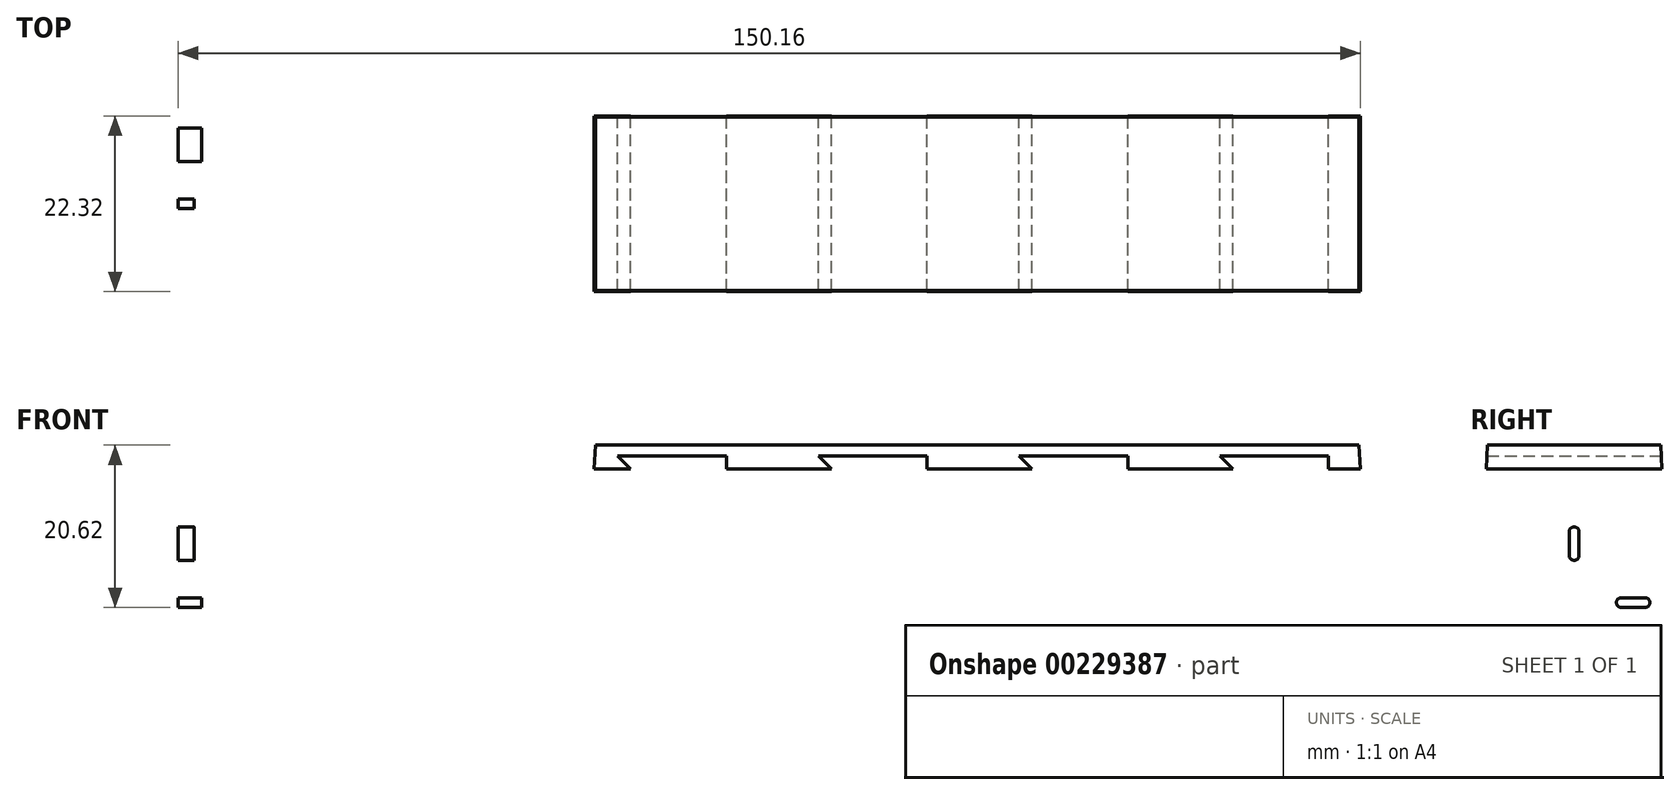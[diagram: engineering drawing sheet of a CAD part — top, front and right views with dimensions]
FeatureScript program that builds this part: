
annotation { "Feature Type Name" : "Feature", "Feature Type Description" : "" }
export const myFeature = defineFeature(function(context is Context, id is Id, definition is map)
    precondition{}
    {
        {
            var Q0;
            Q0=qCreatedBy(makeId("Top.planeOp"),FACE);
            var sketch = newSketch(context, id + "F0", { "sketchPlane" : qUnion([Q0])});
            skLineSegment(sketch, "E0", {"start": v(-75, 15.5) * mm, "end": v(-75, -15.5) * mm});
            skLineSegment(sketch, "E1", {"start": v(-75, -15.5) * mm, "end": v(75, -14) * mm});
            skLineSegment(sketch, "E2", {"start": v(75, -14) * mm, "end": v(75, 14) * mm});
            skLineSegment(sketch, "E3", {"start": v(75, 14) * mm, "end": v(-75, 15.5) * mm});
            skPoint(sketch, "E4", {"position": v(-75, 0) * mm});
            skPoint(sketch, "E5", {"position": v(75, 0) * mm});
            skPoint(sketch, "E6", {"position": v(0, 14.75) * mm});
            skLineSegment(sketch, "E7.0", {"start": v(-72, -12.47) * mm, "end": v(75, -11) * mm});
            skLineSegment(sketch, "E7.1", {"start": v(-72, 12.47) * mm, "end": v(-72, -12.47) * mm});
            skLineSegment(sketch, "E7.2", {"start": v(75, 11) * mm, "end": v(-72, 12.47) * mm});
            skLineSegment(sketch, "E8", {"start": v(-22, 11.97) * mm, "end": v(-22, -11.97) * mm});
            skSolve(sketch);
        }
        {
            var Q0;
            Q0=qCreatedBy(makeId("Top.planeOp"),FACE);
            cPlane(context, id + "F1", {"entities" : qUnion([Q0]), "cplaneType" : CPlaneType.OFFSET, "offset" : 40 * mm, "width" : 150 * mm, "height" : 150 * mm});
        }
        {
            var Q0;
            Q0=qCreatedBy(id+"F1.planeOp",FACE);
            var sketch = newSketch(context, id + "F8", { "sketchPlane" : qUnion([Q0])});
            skLineSegment(sketch, "E9.0", {"start": v(75, -14) * mm, "end": v(75, 14) * mm});
            skPoint(sketch, "E10.0", {"position": v(-75, 0) * mm});
            skLineSegment(sketch, "E11", {"start": v(75, 14) * mm, "end": v(-75, 14) * mm});
            skLineSegment(sketch, "E12", {"start": v(-75, -14) * mm, "end": v(75, -14) * mm});
            skLineSegment(sketch, "E13", {"start": v(-75, 14) * mm, "end": v(-75, -14) * mm});
            skLineSegment(sketch, "E14.0", {"start": v(-72, -11) * mm, "end": v(75, -11) * mm});
            skLineSegment(sketch, "E14.1", {"start": v(-72, 11) * mm, "end": v(-72, -11) * mm});
            skLineSegment(sketch, "E14.2", {"start": v(75, 11) * mm, "end": v(-72, 11) * mm});
            skLineSegment(sketch, "E15", {"start": v(-22, 11) * mm, "end": v(-22, -11) * mm});
            skSolve(sketch);
        }
        {
            var Q0;
            Q0=makeQuery(id+"F0.imprint","IMPRINT",FACE,{"disambiguationData":[TD([[makeQuery(id+"F0.imprint","IMPRINT",EDGE,{"derivedFrom":sQuery(id+"F0.wireOp",EDGE,"E0")}),1.0]])]});
            var Q1;
            {var subQ1=sQuery(id+"F8.wireOp",EDGE,"E11");Q1=makeQuery(id+"F8.imprint","IMPRINT",FACE,{"disambiguationData":[TD([[makeQuery(id+"F8.imprint","IMPRINT",EDGE,{"derivedFrom":subQ1}),1.0]])]});}
            loft(context, id + "F2", {"sheetProfilesArray" : [{ "sheetProfileEntities" : qUnion([Q0]) }, { "sheetProfileEntities" : qUnion([Q1]) }]});
        }
        {
            var Q0;
            {var subQ0=sQuery(id+"F0.wireOp",EDGE,"E7.1");Q0=makeQuery(id+"F0.imprint","IMPRINT",FACE,{"disambiguationData":[TD([[makeQuery(id+"F0.imprint","IMPRINT",EDGE,{"derivedFrom":subQ0}),1.0]])]});}
            extrude(context, id + "F9", {"entities" : qUnion([Q0]), "operationType" : NewBodyOperationType.ADD, "depth" : 3 * mm, "hasDraft" : true, "draftAngle" : 3 * degree});
        }
        {
            var Q0;
            Q0=makeQuery(id+"F2.opLoft","SWEPT_FACE",FACE,{"disambiguationData":[OSD([sQuery(id+"F0.wireOp",EDGE,"E0"),sQuery(id+"F0.wireOp",EDGE,"E1"),sQuery(id+"F0.wireOp",EDGE,"E3"),sQuery(id+"F8.wireOp",EDGE,"E11"),sQuery(id+"F8.wireOp",EDGE,"E12"),sQuery(id+"F8.wireOp",EDGE,"E13")])]});
            var sketch = newSketch(context, id + "F3", { "sketchPlane" : qUnion([Q0])});
            skLineSegment(sketch, "E16.0", {"start": v(-14, 40) * mm, "end": v(14, 40) * mm});
            skLineSegment(sketch, "E17.0", {"start": v(15.5, 0) * mm, "end": v(14, 40) * mm});
            skLineSegment(sketch, "E18.0", {"start": v(-15.5, 0) * mm, "end": v(15.5, 0) * mm});
            skLineSegment(sketch, "E19.0", {"start": v(-15.5, 0) * mm, "end": v(-14, 40) * mm});
            skPoint(sketch, "E20", {"position": v(-14.75, 20) * mm});
            skPoint(sketch, "E21", {"position": v(14.75, 20) * mm});
            skPoint(sketch, "E22", {"position": v(0, 40) * mm});
            skPoint(sketch, "E23", {"position": v(0, 0) * mm});
            skPoint(sketch, "E24", {"position": v(0, 20) * mm});
            skCircle(sketch, "E25", {"center": v(0, 20) * mm, "radius": 2.5 * mm});
            skLineSegment(sketch, "E26", {"start": v(0, 26) * mm, "end": v(0, 29) * mm});
            skLineSegment(sketch, "E27", {"start": v(-9, 20) * mm, "end": v(-6, 20) * mm});
            skArc(sketch, "E28.0.startCap", {"start": v(-9, 19.37) * mm, "mid": v(-9.63, 20) * mm, "end": v(-9, 20.62) * mm});
            skArc(sketch, "E28.0.endCap", {"start": v(-6, 20.62) * mm, "mid": v(-5.38, 20) * mm, "end": v(-6, 19.37) * mm});
            skLineSegment(sketch, "E28.0.left", {"start": v(-9, 20.62) * mm, "end": v(-6, 20.62) * mm});
            skLineSegment(sketch, "E28.0.right", {"start": v(-9, 19.37) * mm, "end": v(-6, 19.37) * mm});
            skArc(sketch, "E29.0.startCap", {"start": v(0.62, 26) * mm, "mid": v(0, 25.37) * mm, "end": v(-0.62, 26) * mm});
            skArc(sketch, "E29.0.endCap", {"start": v(-0.62, 29) * mm, "mid": v(0, 29.62) * mm, "end": v(0.62, 29) * mm});
            skLineSegment(sketch, "E29.0.left", {"start": v(-0.62, 26) * mm, "end": v(-0.62, 29) * mm});
            skLineSegment(sketch, "E29.0.right", {"start": v(0.62, 26) * mm, "end": v(0.62, 29) * mm});
            skLineSegment(sketch, "E30", {"start": v(0, 40) * mm, "end": v(0, 0) * mm, "construction": true});
            skLineSegment(sketch, "E31", {"start": v(-14.75, 20) * mm, "end": v(14.75, 20) * mm, "construction": true});
            skArc(sketch, "E32.MirrorCS", {"start": v(9, 19.37) * mm, "mid": v(9.62, 20) * mm, "end": v(9, 20.62) * mm});
            skLineSegment(sketch, "E33.MirrorCS", {"start": v(9, 20.62) * mm, "end": v(6, 20.62) * mm});
            skArc(sketch, "E34.MirrorCS", {"start": v(6, 20.62) * mm, "mid": v(5.37, 20) * mm, "end": v(6, 19.37) * mm});
            skLineSegment(sketch, "E35.MirrorCS", {"start": v(9, 19.37) * mm, "end": v(6, 19.37) * mm});
            skArc(sketch, "E36.MirrorCS", {"start": v(0.63, 14) * mm, "mid": v(0, 14.62) * mm, "end": v(-0.62, 14) * mm});
            skLineSegment(sketch, "E37.MirrorCS", {"start": v(0.63, 14) * mm, "end": v(0.63, 11) * mm});
            skLineSegment(sketch, "E38.MirrorCS", {"start": v(-0.62, 14) * mm, "end": v(-0.62, 11) * mm});
            skArc(sketch, "E39.MirrorCS", {"start": v(-0.62, 11) * mm, "mid": v(0, 10.37) * mm, "end": v(0.63, 11) * mm});
            skSolve(sketch);
        }
        {
            var Q0;
            Q0=makeQuery(id+"F3.imprint","IMPRINT",FACE,{"disambiguationData":[TD([[makeQuery(id+"F3.imprint","IMPRINT",EDGE,{"derivedFrom":sQuery(id+"F3.wireOp",EDGE,"E32.MirrorCS")}),1.0]])]});
            var Q1;
            Q1=makeQuery(id+"F3.imprint","IMPRINT",FACE,{"disambiguationData":[TD([[makeQuery(id+"F3.imprint","IMPRINT",EDGE,{"derivedFrom":sQuery(id+"F3.wireOp",EDGE,"E25")}),1.0]])]});
            var Q2;
            Q2=makeQuery(id+"F3.imprint","IMPRINT",FACE,{"disambiguationData":[TD([[makeQuery(id+"F3.imprint","IMPRINT",EDGE,{"derivedFrom":sQuery(id+"F3.wireOp",EDGE,"E29.0.startCap")}),-1.0]])]});
            var Q3;
            Q3=makeQuery(id+"F3.imprint","IMPRINT",FACE,{"disambiguationData":[TD([[makeQuery(id+"F3.imprint","IMPRINT",EDGE,{"derivedFrom":sQuery(id+"F3.wireOp",EDGE,"E36.MirrorCS")}),1.0]])]});
            var Q4;
            Q4=makeQuery(id+"F3.imprint","IMPRINT",FACE,{"disambiguationData":[TD([[makeQuery(id+"F3.imprint","IMPRINT",EDGE,{"derivedFrom":sQuery(id+"F3.wireOp",EDGE,"E28.0.startCap")}),-1.0]])]});
            extrude(context, id + "F4", {"entities" : qUnion([Q0, Q1, Q2, Q3, Q4]), "operationType" : NewBodyOperationType.REMOVE, "endBound" : BoundingType.UP_TO_NEXT, "oppositeDirection" : true, "depth" : 25 * mm});
        }
        {
            var Q0;
            {var subQ5=sQuery(id+"F8.wireOp",EDGE,"E15");Q0=makeQuery(id+"F8.imprint","IMPRINT",FACE,{"disambiguationData":[TD([[makeQuery(id+"F8.imprint","IMPRINT",EDGE,{"derivedFrom":subQ5}),1.0]])]});}
            extrude(context, id + "F5", {"entities" : qUnion([Q0]), "operationType" : NewBodyOperationType.ADD, "oppositeDirection" : true, "depth" : 3 * mm, "hasDraft" : true, "draftAngle" : 3 * degree});
        }
        {
            var Q0;
            Q0=qCreatedBy(makeId("Front.planeOp"),FACE);
            var sketch = newSketch(context, id + "F6", { "sketchPlane" : qUnion([Q0])});
            skPoint(sketch, "E40.0", {"position": v(-75, 20.63) * mm});
            skLineSegment(sketch, "E41", {"start": v(-75, 20.63) * mm, "end": v(75.05, 20.63) * mm, "construction": true});
            skLineSegment(sketch, "E42.bottom", {"start": v(-75, 20.63) * mm, "end": v(-54.37, 20.63) * mm});
            skLineSegment(sketch, "E42.top", {"start": v(-75, 0) * mm, "end": v(-54.37, 0) * mm});
            skLineSegment(sketch, "E42.left", {"start": v(-75, 20.63) * mm, "end": v(-75, 0) * mm});
            skLineSegment(sketch, "E42.right", {"start": v(-54.37, 20.63) * mm, "end": v(-54.37, 0) * mm});
            skLineSegment(sketch, "E43", {"start": v(-75, 20.63) * mm, "end": v(-54.37, 0) * mm});
            skLineSegment(sketch, "E44.0", {"start": v(-70.17, 18.63) * mm, "end": v(-56.37, 4.83) * mm});
            skLineSegment(sketch, "E44.1", {"start": v(-70.17, 18.63) * mm, "end": v(-56.37, 18.63) * mm});
            skLineSegment(sketch, "E44.2", {"start": v(-56.37, 18.63) * mm, "end": v(-56.37, 4.83) * mm});
            skLineSegment(sketch, "E45.0", {"start": v(-73, 15.8) * mm, "end": v(-73, 2) * mm});
            skLineSegment(sketch, "E45.1", {"start": v(-73, 15.8) * mm, "end": v(-59.2, 2) * mm});
            skLineSegment(sketch, "E45.2", {"start": v(-73, 2) * mm, "end": v(-59.2, 2) * mm});
            skLineSegment(sketch, "E46.0.1.0", {"start": v(-70.17, 38.63) * mm, "end": v(-56.37, 38.63) * mm});
            skLineSegment(sketch, "E46.0.1.1", {"start": v(-73, 35.8) * mm, "end": v(-73, 22) * mm});
            skLineSegment(sketch, "E46.0.1.2", {"start": v(-73, 35.8) * mm, "end": v(-59.2, 22) * mm});
            skLineSegment(sketch, "E46.0.1.3", {"start": v(-56.37, 38.63) * mm, "end": v(-56.37, 24.83) * mm});
            skLineSegment(sketch, "E46.0.1.4", {"start": v(-70.17, 38.63) * mm, "end": v(-56.37, 24.83) * mm});
            skLineSegment(sketch, "E46.0.1.5", {"start": v(-73, 22) * mm, "end": v(-59.2, 22) * mm});
            skLineSegment(sketch, "E46.1.0.0", {"start": v(-44.67, 18.63) * mm, "end": v(-30.87, 18.63) * mm});
            skLineSegment(sketch, "E46.1.0.1", {"start": v(-47.5, 15.8) * mm, "end": v(-47.5, 2) * mm});
            skLineSegment(sketch, "E46.1.0.2", {"start": v(-47.5, 15.8) * mm, "end": v(-33.7, 2) * mm});
            skLineSegment(sketch, "E46.1.0.3", {"start": v(-30.87, 18.63) * mm, "end": v(-30.87, 4.83) * mm});
            skLineSegment(sketch, "E46.1.0.4", {"start": v(-44.67, 18.63) * mm, "end": v(-30.87, 4.83) * mm});
            skLineSegment(sketch, "E46.1.0.5", {"start": v(-47.5, 2) * mm, "end": v(-33.7, 2) * mm});
            skLineSegment(sketch, "E46.1.1.0", {"start": v(-44.67, 38.63) * mm, "end": v(-30.87, 38.63) * mm});
            skLineSegment(sketch, "E46.1.1.1", {"start": v(-47.5, 35.8) * mm, "end": v(-47.5, 22) * mm});
            skLineSegment(sketch, "E46.1.1.2", {"start": v(-47.5, 35.8) * mm, "end": v(-33.7, 22) * mm});
            skLineSegment(sketch, "E46.1.1.3", {"start": v(-30.87, 38.63) * mm, "end": v(-30.87, 24.83) * mm});
            skLineSegment(sketch, "E46.1.1.4", {"start": v(-44.67, 38.63) * mm, "end": v(-30.87, 24.83) * mm});
            skLineSegment(sketch, "E46.1.1.5", {"start": v(-47.5, 22) * mm, "end": v(-33.7, 22) * mm});
            skLineSegment(sketch, "E46.2.0.0", {"start": v(-19.17, 18.63) * mm, "end": v(-5.37, 18.63) * mm});
            skLineSegment(sketch, "E46.2.0.1", {"start": v(-22, 15.8) * mm, "end": v(-22, 2) * mm});
            skLineSegment(sketch, "E46.2.0.2", {"start": v(-22, 15.8) * mm, "end": v(-8.2, 2) * mm});
            skLineSegment(sketch, "E46.2.0.3", {"start": v(-5.37, 18.63) * mm, "end": v(-5.37, 4.83) * mm});
            skLineSegment(sketch, "E46.2.0.4", {"start": v(-19.17, 18.63) * mm, "end": v(-5.37, 4.83) * mm});
            skLineSegment(sketch, "E46.2.0.5", {"start": v(-22, 2) * mm, "end": v(-8.2, 2) * mm});
            skLineSegment(sketch, "E46.2.1.0", {"start": v(-19.17, 38.63) * mm, "end": v(-5.37, 38.63) * mm});
            skLineSegment(sketch, "E46.2.1.1", {"start": v(-22, 35.8) * mm, "end": v(-22, 22) * mm});
            skLineSegment(sketch, "E46.2.1.2", {"start": v(-22, 35.8) * mm, "end": v(-8.2, 22) * mm});
            skLineSegment(sketch, "E46.2.1.3", {"start": v(-5.37, 38.63) * mm, "end": v(-5.37, 24.83) * mm});
            skLineSegment(sketch, "E46.2.1.4", {"start": v(-19.17, 38.63) * mm, "end": v(-5.37, 24.83) * mm});
            skLineSegment(sketch, "E46.2.1.5", {"start": v(-22, 22) * mm, "end": v(-8.2, 22) * mm});
            skLineSegment(sketch, "E46.3.0.0", {"start": v(6.33, 18.63) * mm, "end": v(20.13, 18.63) * mm});
            skLineSegment(sketch, "E46.3.0.1", {"start": v(3.5, 15.8) * mm, "end": v(3.5, 2) * mm});
            skLineSegment(sketch, "E46.3.0.2", {"start": v(3.5, 15.8) * mm, "end": v(17.3, 2) * mm});
            skLineSegment(sketch, "E46.3.0.3", {"start": v(20.13, 18.63) * mm, "end": v(20.13, 4.83) * mm});
            skLineSegment(sketch, "E46.3.0.4", {"start": v(6.33, 18.63) * mm, "end": v(20.13, 4.83) * mm});
            skLineSegment(sketch, "E46.3.0.5", {"start": v(3.5, 2) * mm, "end": v(17.3, 2) * mm});
            skLineSegment(sketch, "E46.3.1.0", {"start": v(6.33, 38.63) * mm, "end": v(20.13, 38.63) * mm});
            skLineSegment(sketch, "E46.3.1.1", {"start": v(3.5, 35.8) * mm, "end": v(3.5, 22) * mm});
            skLineSegment(sketch, "E46.3.1.2", {"start": v(3.5, 35.8) * mm, "end": v(17.3, 22) * mm});
            skLineSegment(sketch, "E46.3.1.3", {"start": v(20.13, 38.63) * mm, "end": v(20.13, 24.83) * mm});
            skLineSegment(sketch, "E46.3.1.4", {"start": v(6.33, 38.63) * mm, "end": v(20.13, 24.83) * mm});
            skLineSegment(sketch, "E46.3.1.5", {"start": v(3.5, 22) * mm, "end": v(17.3, 22) * mm});
            skLineSegment(sketch, "E46.4.0.0", {"start": v(31.83, 18.63) * mm, "end": v(45.63, 18.63) * mm});
            skLineSegment(sketch, "E46.4.0.1", {"start": v(29, 15.8) * mm, "end": v(29, 2) * mm});
            skLineSegment(sketch, "E46.4.0.2", {"start": v(29, 15.8) * mm, "end": v(42.8, 2) * mm});
            skLineSegment(sketch, "E46.4.0.3", {"start": v(45.63, 18.63) * mm, "end": v(45.63, 4.83) * mm});
            skLineSegment(sketch, "E46.4.0.4", {"start": v(31.83, 18.63) * mm, "end": v(45.63, 4.83) * mm});
            skLineSegment(sketch, "E46.4.0.5", {"start": v(29, 2) * mm, "end": v(42.8, 2) * mm});
            skLineSegment(sketch, "E46.4.1.0", {"start": v(31.83, 38.63) * mm, "end": v(45.63, 38.63) * mm});
            skLineSegment(sketch, "E46.4.1.1", {"start": v(29, 35.8) * mm, "end": v(29, 22) * mm});
            skLineSegment(sketch, "E46.4.1.2", {"start": v(29, 35.8) * mm, "end": v(42.8, 22) * mm});
            skLineSegment(sketch, "E46.4.1.3", {"start": v(45.63, 38.63) * mm, "end": v(45.63, 24.83) * mm});
            skLineSegment(sketch, "E46.4.1.4", {"start": v(31.83, 38.63) * mm, "end": v(45.63, 24.83) * mm});
            skLineSegment(sketch, "E46.4.1.5", {"start": v(29, 22) * mm, "end": v(42.8, 22) * mm});
            skLineSegment(sketch, "E46.5.0.0", {"start": v(57.33, 18.63) * mm, "end": v(71.13, 18.63) * mm});
            skLineSegment(sketch, "E46.5.0.1", {"start": v(54.5, 15.8) * mm, "end": v(54.5, 2) * mm});
            skLineSegment(sketch, "E46.5.0.2", {"start": v(54.5, 15.8) * mm, "end": v(68.3, 2) * mm});
            skLineSegment(sketch, "E46.5.0.3", {"start": v(71.13, 18.63) * mm, "end": v(71.13, 4.83) * mm});
            skLineSegment(sketch, "E46.5.0.4", {"start": v(57.33, 18.63) * mm, "end": v(71.13, 4.83) * mm});
            skLineSegment(sketch, "E46.5.0.5", {"start": v(54.5, 2) * mm, "end": v(68.3, 2) * mm});
            skLineSegment(sketch, "E46.5.1.0", {"start": v(57.33, 38.63) * mm, "end": v(71.13, 38.63) * mm});
            skLineSegment(sketch, "E46.5.1.1", {"start": v(54.5, 35.8) * mm, "end": v(54.5, 22) * mm});
            skLineSegment(sketch, "E46.5.1.2", {"start": v(54.5, 35.8) * mm, "end": v(68.3, 22) * mm});
            skLineSegment(sketch, "E46.5.1.3", {"start": v(71.13, 38.63) * mm, "end": v(71.13, 24.83) * mm});
            skLineSegment(sketch, "E46.5.1.4", {"start": v(57.33, 38.63) * mm, "end": v(71.13, 24.83) * mm});
            skLineSegment(sketch, "E46.5.1.5", {"start": v(54.5, 22) * mm, "end": v(68.3, 22) * mm});
            skLineSegment(sketch, "E46.direction1", {"start": v(-73, 2) * mm, "end": v(-47.5, 2) * mm, "construction": true});
            skLineSegment(sketch, "E46.direction2", {"start": v(-73, 2) * mm, "end": v(-73, 22) * mm, "construction": true});
            skSolve(sketch);
        }
        {
            var Q0;
            Q0=makeQuery(id+"F6.imprint","IMPRINT",FACE,{"disambiguationData":[TD([[makeQuery(id+"F6.imprint","IMPRINT",EDGE,{"derivedFrom":sQuery(id+"F6.wireOp",EDGE,"E46.0.1.1")}),1.0]])]});
            var Q1;
            Q1=makeQuery(id+"F6.imprint","IMPRINT",FACE,{"disambiguationData":[TD([[makeQuery(id+"F6.imprint","IMPRINT",EDGE,{"derivedFrom":sQuery(id+"F6.wireOp",EDGE,"E46.0.1.0")}),-1.0]])]});
            var Q2;
            Q2=makeQuery(id+"F6.imprint","IMPRINT",FACE,{"disambiguationData":[TD([[makeQuery(id+"F6.imprint","IMPRINT",EDGE,{"derivedFrom":sQuery(id+"F6.wireOp",EDGE,"E44.0")}),1.0]])]});
            var Q3;
            Q3=makeQuery(id+"F6.imprint","IMPRINT",FACE,{"disambiguationData":[TD([[makeQuery(id+"F6.imprint","IMPRINT",EDGE,{"derivedFrom":sQuery(id+"F6.wireOp",EDGE,"E45.0")}),1.0]])]});
            var Q4;
            Q4=makeQuery(id+"F6.imprint","IMPRINT",FACE,{"disambiguationData":[TD([[makeQuery(id+"F6.imprint","IMPRINT",EDGE,{"derivedFrom":sQuery(id+"F6.wireOp",EDGE,"E46.1.1.0")}),-1.0]])]});
            var Q5;
            Q5=makeQuery(id+"F6.imprint","IMPRINT",FACE,{"disambiguationData":[TD([[makeQuery(id+"F6.imprint","IMPRINT",EDGE,{"derivedFrom":sQuery(id+"F6.wireOp",EDGE,"E46.1.1.1")}),1.0]])]});
            var Q6;
            Q6=makeQuery(id+"F6.imprint","IMPRINT",FACE,{"disambiguationData":[TD([[makeQuery(id+"F6.imprint","IMPRINT",EDGE,{"derivedFrom":sQuery(id+"F6.wireOp",EDGE,"E46.1.0.0")}),-1.0]])]});
            var Q7;
            Q7=makeQuery(id+"F6.imprint","IMPRINT",FACE,{"disambiguationData":[TD([[makeQuery(id+"F6.imprint","IMPRINT",EDGE,{"derivedFrom":sQuery(id+"F6.wireOp",EDGE,"E46.1.0.1")}),1.0]])]});
            var Q8;
            Q8=makeQuery(id+"F6.imprint","IMPRINT",FACE,{"disambiguationData":[TD([[makeQuery(id+"F6.imprint","IMPRINT",EDGE,{"derivedFrom":sQuery(id+"F6.wireOp",EDGE,"E46.2.0.1")}),1.0]])]});
            var Q9;
            Q9=makeQuery(id+"F6.imprint","IMPRINT",FACE,{"disambiguationData":[TD([[makeQuery(id+"F6.imprint","IMPRINT",EDGE,{"derivedFrom":sQuery(id+"F6.wireOp",EDGE,"E46.2.0.0")}),-1.0]])]});
            var Q10;
            Q10=makeQuery(id+"F6.imprint","IMPRINT",FACE,{"disambiguationData":[TD([[makeQuery(id+"F6.imprint","IMPRINT",EDGE,{"derivedFrom":sQuery(id+"F6.wireOp",EDGE,"E46.2.1.1")}),1.0]])]});
            var Q11;
            Q11=makeQuery(id+"F6.imprint","IMPRINT",FACE,{"disambiguationData":[TD([[makeQuery(id+"F6.imprint","IMPRINT",EDGE,{"derivedFrom":sQuery(id+"F6.wireOp",EDGE,"E46.2.1.0")}),-1.0]])]});
            var Q12;
            Q12=makeQuery(id+"F6.imprint","IMPRINT",FACE,{"disambiguationData":[TD([[makeQuery(id+"F6.imprint","IMPRINT",EDGE,{"derivedFrom":sQuery(id+"F6.wireOp",EDGE,"E46.3.1.1")}),1.0]])]});
            var Q13;
            Q13=makeQuery(id+"F6.imprint","IMPRINT",FACE,{"disambiguationData":[TD([[makeQuery(id+"F6.imprint","IMPRINT",EDGE,{"derivedFrom":sQuery(id+"F6.wireOp",EDGE,"E46.3.1.0")}),-1.0]])]});
            var Q14;
            Q14=makeQuery(id+"F6.imprint","IMPRINT",FACE,{"disambiguationData":[TD([[makeQuery(id+"F6.imprint","IMPRINT",EDGE,{"derivedFrom":sQuery(id+"F6.wireOp",EDGE,"E46.3.0.0")}),-1.0]])]});
            var Q15;
            Q15=makeQuery(id+"F6.imprint","IMPRINT",FACE,{"disambiguationData":[TD([[makeQuery(id+"F6.imprint","IMPRINT",EDGE,{"derivedFrom":sQuery(id+"F6.wireOp",EDGE,"E46.3.0.1")}),1.0]])]});
            var Q16;
            Q16=makeQuery(id+"F6.imprint","IMPRINT",FACE,{"disambiguationData":[TD([[makeQuery(id+"F6.imprint","IMPRINT",EDGE,{"derivedFrom":sQuery(id+"F6.wireOp",EDGE,"E46.4.1.1")}),1.0]])]});
            var Q17;
            Q17=makeQuery(id+"F6.imprint","IMPRINT",FACE,{"disambiguationData":[TD([[makeQuery(id+"F6.imprint","IMPRINT",EDGE,{"derivedFrom":sQuery(id+"F6.wireOp",EDGE,"E46.4.1.0")}),-1.0]])]});
            var Q18;
            Q18=makeQuery(id+"F6.imprint","IMPRINT",FACE,{"disambiguationData":[TD([[makeQuery(id+"F6.imprint","IMPRINT",EDGE,{"derivedFrom":sQuery(id+"F6.wireOp",EDGE,"E46.4.0.0")}),-1.0]])]});
            var Q19;
            Q19=makeQuery(id+"F6.imprint","IMPRINT",FACE,{"disambiguationData":[TD([[makeQuery(id+"F6.imprint","IMPRINT",EDGE,{"derivedFrom":sQuery(id+"F6.wireOp",EDGE,"E46.4.0.1")}),1.0]])]});
            var Q20;
            Q20=makeQuery(id+"F6.imprint","IMPRINT",FACE,{"disambiguationData":[TD([[makeQuery(id+"F6.imprint","IMPRINT",EDGE,{"derivedFrom":sQuery(id+"F6.wireOp",EDGE,"E46.5.0.1")}),1.0]])]});
            var Q21;
            Q21=makeQuery(id+"F6.imprint","IMPRINT",FACE,{"disambiguationData":[TD([[makeQuery(id+"F6.imprint","IMPRINT",EDGE,{"derivedFrom":sQuery(id+"F6.wireOp",EDGE,"E46.5.0.0")}),-1.0]])]});
            var Q22;
            Q22=makeQuery(id+"F6.imprint","IMPRINT",FACE,{"disambiguationData":[TD([[makeQuery(id+"F6.imprint","IMPRINT",EDGE,{"derivedFrom":sQuery(id+"F6.wireOp",EDGE,"E46.5.1.1")}),1.0]])]});
            var Q23;
            Q23=makeQuery(id+"F6.imprint","IMPRINT",FACE,{"disambiguationData":[TD([[makeQuery(id+"F6.imprint","IMPRINT",EDGE,{"derivedFrom":sQuery(id+"F6.wireOp",EDGE,"E46.5.1.0")}),-1.0]])]});
            extrude(context, id + "F10", {"entities" : qUnion([Q0, Q1, Q2, Q3, Q4, Q5, Q6, Q7, Q8, Q9, Q10, Q11, Q12, Q13, Q14, Q15, Q16, Q17, Q18, Q19, Q20, Q21, Q22, Q23]), "operationType" : NewBodyOperationType.REMOVE, "endBound" : BoundingType.THROUGH_ALL, "depth" : 25 * mm, "hasSecondDirection" : true, "secondDirectionBound" : SecondDirectionBoundingType.THROUGH_ALL, "secondDirectionOppositeDirection" : true, "secondDirectionDepth" : 25 * mm});
        }
        {
            var Q0;
            Q0=qCreatedBy(makeId("Front.planeOp"),FACE);
            var sketch = newSketch(context, id + "F7", { "sketchPlane" : qUnion([Q0])});
            skLineSegment(sketch, "E47.bottom", {"start": v(-60, 0) * mm, "end": v(-43, 0) * mm});
            skLineSegment(sketch, "E47.top", {"start": v(-60, 6) * mm, "end": v(-43, 6) * mm});
            skLineSegment(sketch, "E47.left", {"start": v(-60, 0) * mm, "end": v(-60, 6) * mm});
            skLineSegment(sketch, "E47.right", {"start": v(-43, 0) * mm, "end": v(-43, 6) * mm});
            skSolve(sketch);
        }
        {
            var Q0;
            Q0=makeQuery(id+"F7.imprint","IMPRINT",FACE,{"disambiguationData":[TD([[makeQuery(id+"F7.imprint","IMPRINT",EDGE,{"derivedFrom":sQuery(id+"F7.wireOp",EDGE,"E47.bottom")}),1.0]])]});
            extrude(context, id + "F11", {"entities" : qUnion([Q0]), "operationType" : NewBodyOperationType.REMOVE, "endBound" : BoundingType.THROUGH_ALL, "oppositeDirection" : true, "depth" : 25 * mm, "hasSecondDirection" : true, "secondDirectionBound" : SecondDirectionBoundingType.THROUGH_ALL, "secondDirectionOppositeDirection" : false, "secondDirectionDepth" : 25 * mm});
        }
    });
